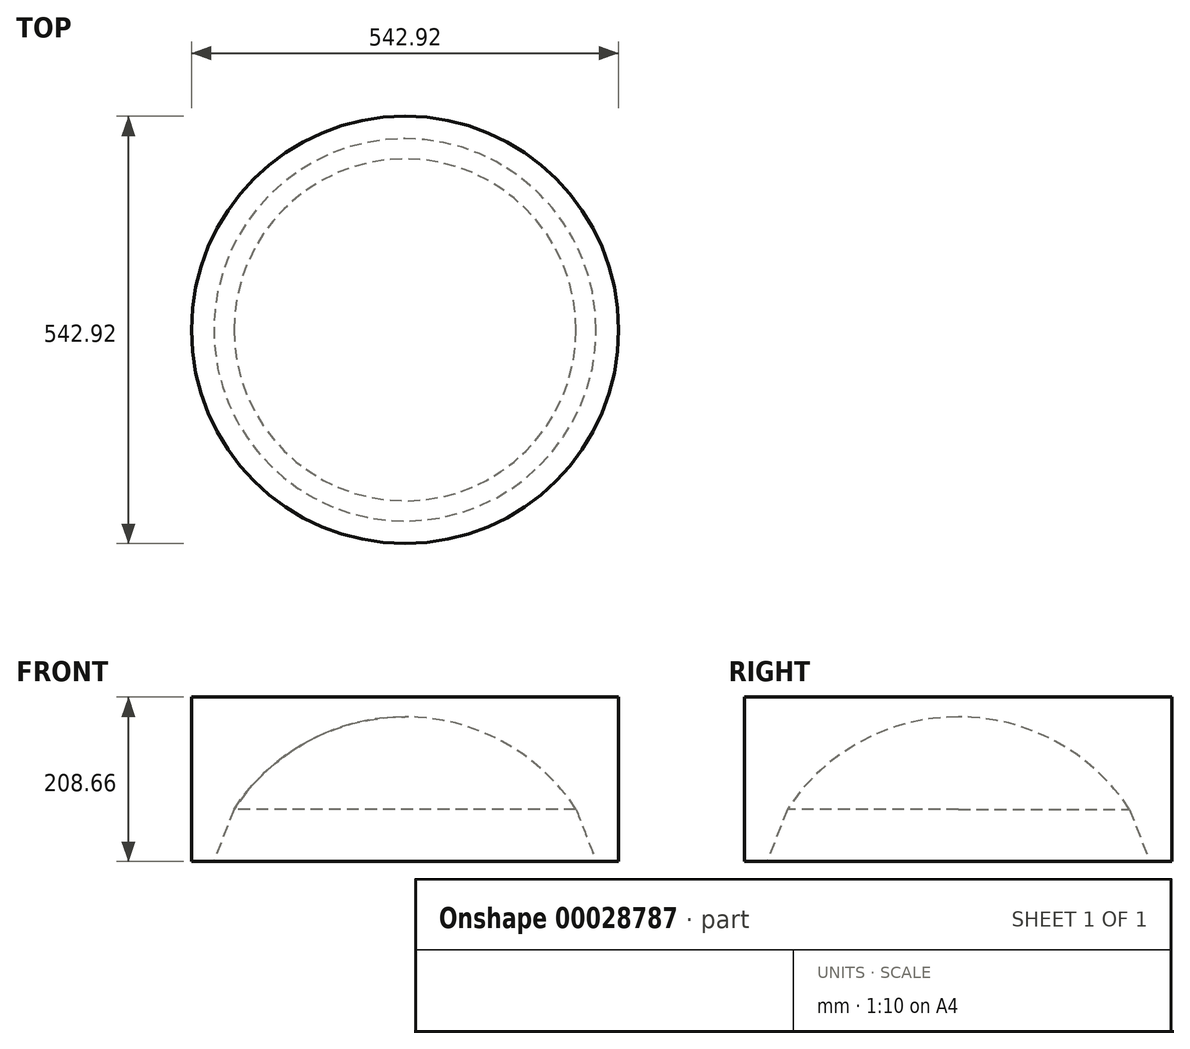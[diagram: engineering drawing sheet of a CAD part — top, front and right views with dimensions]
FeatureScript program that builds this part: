
annotation { "Feature Type Name" : "Feature", "Feature Type Description" : "" }
export const myFeature = defineFeature(function(context is Context, id is Id, definition is map)
    precondition{}
    {
        {
            var Q0;
            Q0=qCreatedBy(makeId("Front.planeOp"),FACE);
            var sketch = newSketch(context, id + "F0", { "sketchPlane" : qUnion([Q0])});
            skArc(sketch, "E0", {"start": v(228.6, 142.24) * mm, "mid": v(228.51, 142.38) * mm, "end": v(228.42, 142.53) * mm});
            skLineSegment(sketch, "E1", {"start": v(0, 269.24) * mm, "end": v(0, -269.24) * mm, "construction": true});
            skLineSegment(sketch, "E2", {"start": v(228.6, 142.53) * mm, "end": v(228.42, 142.53) * mm, "construction": true});
            skLineSegment(sketch, "E3", {"start": v(-279, 76.33) * mm, "end": v(507.36, 76.33) * mm, "construction": true});
            skLineSegment(sketch, "E4", {"start": v(-254, 174.53) * mm, "end": v(-254, 8.55) * mm, "construction": true});
            skArc(sketch, "E5.trimOffspring", {"start": v(0, 259.85) * mm, "mid": v(-123.46, 228.64) * mm, "end": v(-217.27, 142.53) * mm});
            skLineSegment(sketch, "E6", {"start": v(-217.27, 142.53) * mm, "end": v(-242.85, 76.33) * mm});
            skLineSegment(sketch, "E7", {"start": v(-254, 76.33) * mm, "end": v(-242.85, 76.33) * mm});
            skLineSegment(sketch, "E8", {"start": v(0, 269.24) * mm, "end": v(0, 259.85) * mm});
            skPoint(sketch, "E9.orphan", {"position": v(232.09, 76.33) * mm});
            skLineSegment(sketch, "E10", {"start": v(0, 259.85) * mm, "end": v(-183.52, 76.33) * mm, "construction": true});
            skLineSegment(sketch, "E11.top", {"start": v(0, 284.99) * mm, "end": v(-271.46, 284.99) * mm});
            skLineSegment(sketch, "E11.left", {"start": v(0, 269.24) * mm, "end": v(0, 284.99) * mm});
            skLineSegment(sketch, "E11.right", {"start": v(-271.46, 269.24) * mm, "end": v(-271.46, 284.99) * mm});
            skLineSegment(sketch, "E12.bottom", {"start": v(-271.46, 284.99) * mm, "end": v(-242.85, 284.99) * mm});
            skLineSegment(sketch, "E12.top", {"start": v(-271.46, 76.33) * mm, "end": v(-242.85, 76.33) * mm});
            skLineSegment(sketch, "E12.left", {"start": v(-271.46, 284.99) * mm, "end": v(-271.46, 76.33) * mm});
            skSolve(sketch);
        }
        {
            var Q0;
            Q0=makeQuery(id+"F0.imprint","IMPRINT",FACE,{"disambiguationData":[TD([[makeQuery(id+"F0.imprint","IMPRINT",EDGE,{"derivedFrom":sQuery(id+"F0.wireOp",EDGE,"E5.trimOffspring")}),-1.0]])]});
            var Q1;
            Q1=sQuery(id+"F0.wireOp",EDGE,"E1");
            revolve(context, id + "F1", {"entities" : qUnion([Q0]), "axis" : qUnion([Q1]), "revolveType" : RevolveType.FULL});
        }
    });
